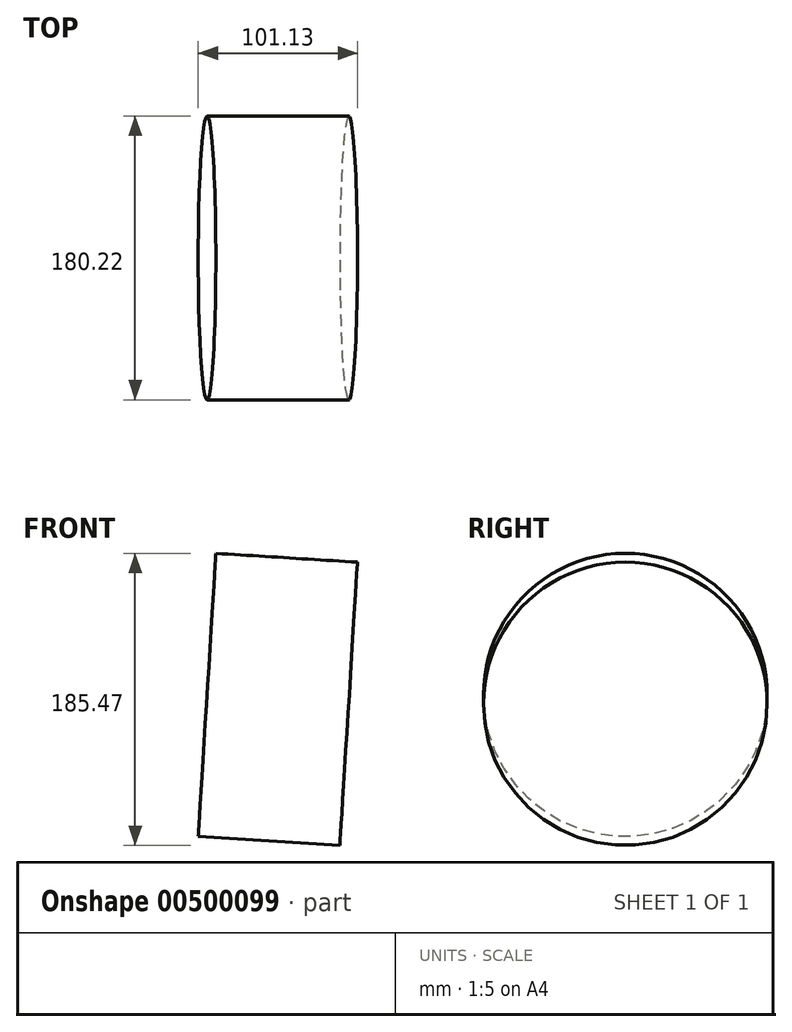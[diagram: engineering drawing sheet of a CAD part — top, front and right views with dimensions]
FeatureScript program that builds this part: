
annotation { "Feature Type Name" : "Feature", "Feature Type Description" : "" }
export const myFeature = defineFeature(function(context is Context, id is Id, definition is map)
    precondition{}
    {
        {
            var Q0;
            Q0=qCreatedBy(makeId("Front.planeOp"),FACE);
            var sketch = newSketch(context, id + "F0", { "sketchPlane" : qUnion([Q0])});
            skCircle(sketch, "E0.cCircle", {"center": v(0, 0) * mm, "radius": 63.72 * mm, "construction": true});
            skLineSegment(sketch, "E0.0", {"start": v(-42.17, 47.77) * mm, "end": v(47.77, 42.17) * mm});
            skLineSegment(sketch, "E0.1", {"start": v(47.77, 42.17) * mm, "end": v(42.17, -47.77) * mm});
            skLineSegment(sketch, "E0.2", {"start": v(42.17, -47.77) * mm, "end": v(-47.77, -42.17) * mm});
            skLineSegment(sketch, "E0.3", {"start": v(-47.77, -42.17) * mm, "end": v(-42.17, 47.77) * mm});
            skSolve(sketch);
        }
        {
            var Q0;
            Q0=makeQuery(id+"F0.imprint","IMPRINT",FACE,{"disambiguationData":[TD([[makeQuery(id+"F0.imprint","IMPRINT",EDGE,{"derivedFrom":sQuery(id+"F0.wireOp",EDGE,"E0.0")}),-1.0]])]});
            var Q1;
            Q1=sQuery(id+"F0.wireOp",EDGE,"E0.0");
            revolve(context, id + "F1", {"entities" : qUnion([Q0]), "axis" : qUnion([Q1]), "revolveType" : RevolveType.FULL});
        }
    });
